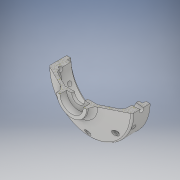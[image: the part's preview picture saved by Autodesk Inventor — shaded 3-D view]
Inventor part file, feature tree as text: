
AUTODESK INVENTOR PART (.ipt)
format: ipt  version: 2018 (Build 220112000, 112)  size: 351,232 bytes
history: native  units: mm
features: sketch x4, revolve x2, extrude x1, hole x1, other x1, pattern_circular x1
ambient origin geometry x8: Origin, YZ Plane, XZ Plane, XY Plane, X Axis, Y Axis, Z Axis, Center Point
bodies: Solid1 (feature_tree)
feature tree (10):
  revolve  "Revolution1"  [1 undecoded]
  extrude  "Extrusion1"  Depth=4.0mm
  hole  "Hole1"  [1 undecoded]
  revolve  "Revolution2"  [1 undecoded]
  other  "Work Axis1"
  pattern_circular  "Circular Pattern1"  [2 undecoded]
  sketch  "Sketch1"  dims[d0=50.0mm d1=45.0mm]
  sketch  "Sketch2"  dims[d2=40.5mm d3=4.0mm]
  sketch  "Sketch3"  dims[d4=32.5mm d5=44.0mm]
  sketch  "Sketch4"  dims[d6=3.5mm d7=18.0mm d8=14.0mm d9=4.63734mm d10=8.0mm d11=3.5mm d12=8.0mm d13=3.0mm d14=90.0deg d15=5.0mm d16=7.0mm d17=9.21mm d18=10.0mm d19=16.5mm d20=59.5mm d21=0.0mm d22=2.25mm d23=4.0mm d24=6.0mm d25=4.0mm d26=2.0mm d27=90.0deg d28=24.5mm d29=0.0mm d30=3.5mm d31=19.0mm d32=5.0mm d33=90.0deg d34=70.0mm d35=360.0deg]
note: 5 required parameter values undecoded (feature->parameter linkage not recoverable at this tier; creation-order binding heuristic only, values carry confidence <= 0.55)